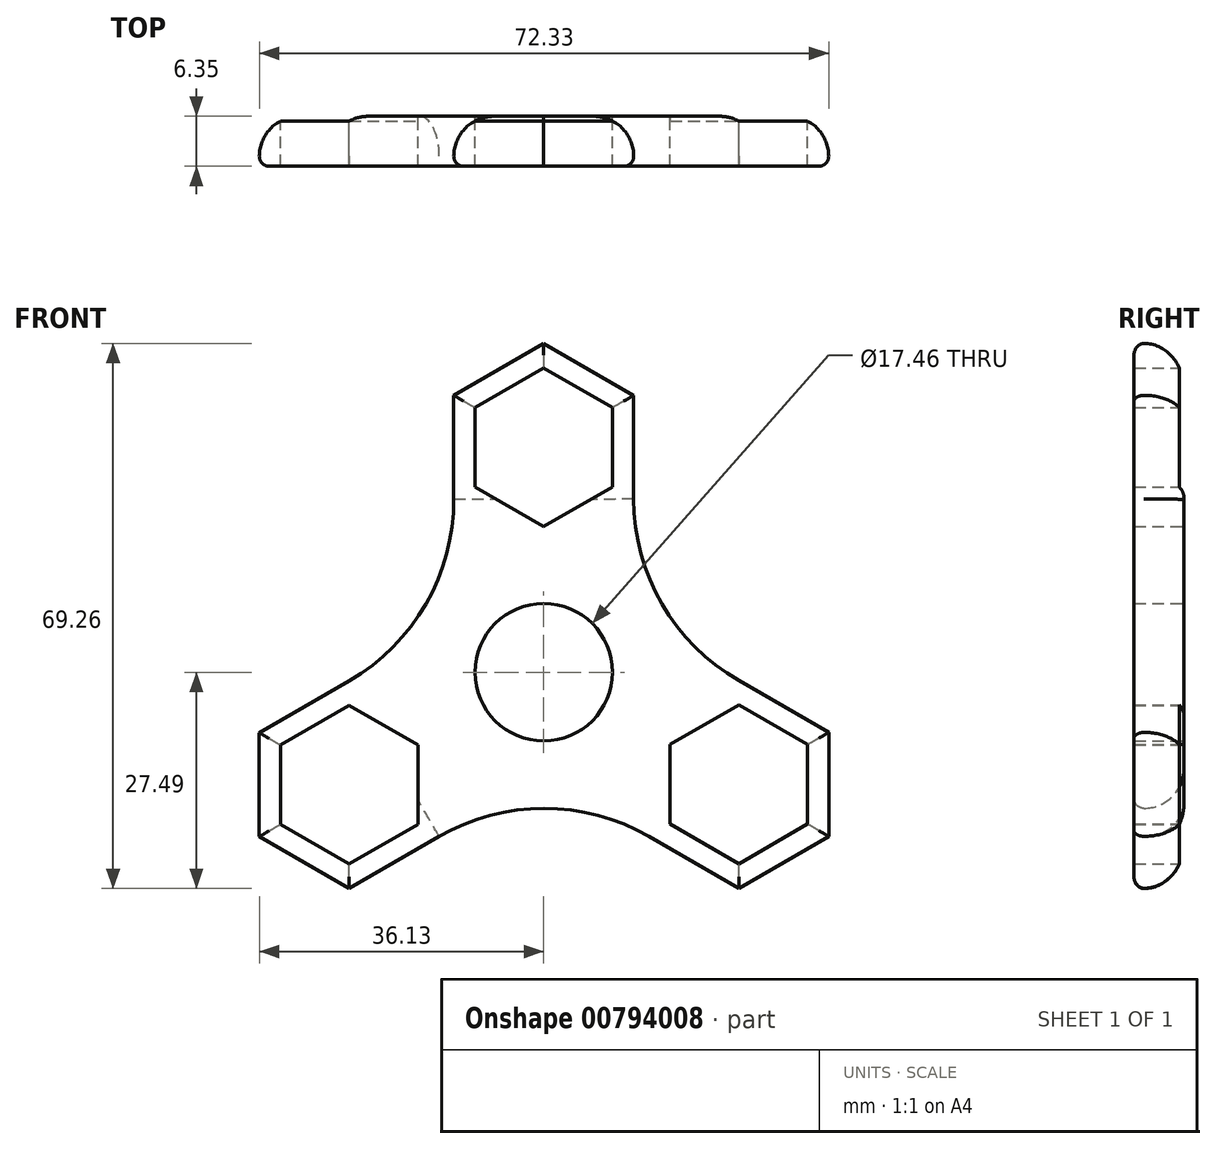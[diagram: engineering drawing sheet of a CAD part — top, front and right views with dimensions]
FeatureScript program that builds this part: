
annotation { "Feature Type Name" : "Feature", "Feature Type Description" : "" }
export const myFeature = defineFeature(function(context is Context, id is Id, definition is map)
    precondition{}
    {
        {
            var Q0;
            Q0=qCreatedBy(makeId("Front.planeOp"),FACE);
            var sketch = newSketch(context, id + "F0", { "sketchPlane" : qUnion([Q0])});
            skCircle(sketch, "E0", {"center": v(0, 0) * mm, "radius": 8.73 * mm});
            skCircle(sketch, "E1", {"center": v(0, 0) * mm, "radius": 14.29 * mm});
            skCircle(sketch, "E2.cCircle", {"center": v(0, 28.58) * mm, "radius": 8.74 * mm, "construction": true});
            skLineSegment(sketch, "E2.0", {"start": v(-8.74, 23.53) * mm, "end": v(-8.74, 33.62) * mm});
            skLineSegment(sketch, "E2.1", {"start": v(-8.74, 33.62) * mm, "end": v(0, 38.66) * mm});
            skLineSegment(sketch, "E2.2", {"start": v(0, 38.66) * mm, "end": v(8.74, 33.62) * mm});
            skLineSegment(sketch, "E2.3", {"start": v(8.74, 33.62) * mm, "end": v(8.74, 23.53) * mm});
            skLineSegment(sketch, "E2.4", {"start": v(8.74, 23.53) * mm, "end": v(0, 18.49) * mm});
            skLineSegment(sketch, "E2.5", {"start": v(0, 18.49) * mm, "end": v(-8.74, 23.53) * mm});
            skPoint(sketch, "E2.0.midPoint", {"position": v(-8.74, 28.58) * mm});
            skCircle(sketch, "E3.cCircle", {"center": v(0, 28.58) * mm, "radius": 11.43 * mm, "construction": true});
            skLineSegment(sketch, "E3.0", {"start": v(-11.43, 21.98) * mm, "end": v(-11.43, 35.17) * mm});
            skLineSegment(sketch, "E3.1", {"start": v(-11.43, 35.17) * mm, "end": v(0, 41.77) * mm});
            skLineSegment(sketch, "E3.2", {"start": v(0, 41.77) * mm, "end": v(11.43, 35.17) * mm});
            skLineSegment(sketch, "E3.3", {"start": v(11.43, 35.17) * mm, "end": v(11.43, 21.98) * mm});
            skLineSegment(sketch, "E3.4", {"start": v(11.43, 21.98) * mm, "end": v(0, 15.38) * mm});
            skLineSegment(sketch, "E3.5", {"start": v(0, 15.38) * mm, "end": v(-11.43, 21.98) * mm});
            skPoint(sketch, "E3.0.midPoint", {"position": v(-11.43, 28.58) * mm});
            skPoint(sketch, "E4.1.0", {"position": v(-18.99, -24.19) * mm});
            skCircle(sketch, "E4.1.1", {"center": v(-24.7, -14.29) * mm, "radius": 8.74 * mm, "construction": true});
            skLineSegment(sketch, "E4.1.2", {"start": v(-33.44, -19.33) * mm, "end": v(-33.44, -9.24) * mm});
            skLineSegment(sketch, "E4.1.3", {"start": v(-13.27, -7.69) * mm, "end": v(-13.27, -20.89) * mm});
            skLineSegment(sketch, "E4.1.4", {"start": v(-24.7, -1.09) * mm, "end": v(-13.27, -7.69) * mm});
            skLineSegment(sketch, "E4.1.5", {"start": v(-36.13, -7.69) * mm, "end": v(-24.7, -1.09) * mm});
            skLineSegment(sketch, "E4.1.6", {"start": v(-24.7, -24.38) * mm, "end": v(-33.44, -19.33) * mm});
            skLineSegment(sketch, "E4.1.7", {"start": v(-33.44, -9.24) * mm, "end": v(-24.7, -4.2) * mm});
            skLineSegment(sketch, "E4.1.8", {"start": v(-15.96, -9.24) * mm, "end": v(-15.96, -19.33) * mm});
            skCircle(sketch, "E4.1.9", {"center": v(-24.7, -14.29) * mm, "radius": 11.43 * mm, "construction": true});
            skLineSegment(sketch, "E4.1.10", {"start": v(-13.27, -20.89) * mm, "end": v(-24.7, -27.49) * mm});
            skLineSegment(sketch, "E4.1.11", {"start": v(-24.7, -27.49) * mm, "end": v(-36.13, -20.89) * mm});
            skLineSegment(sketch, "E4.1.12", {"start": v(-36.13, -20.89) * mm, "end": v(-36.13, -7.69) * mm});
            skPoint(sketch, "E4.1.13", {"position": v(-20.33, -21.85) * mm});
            skLineSegment(sketch, "E4.1.14", {"start": v(-15.96, -19.33) * mm, "end": v(-24.7, -24.38) * mm});
            skLineSegment(sketch, "E4.1.15", {"start": v(-24.7, -4.2) * mm, "end": v(-15.96, -9.24) * mm});
            skPoint(sketch, "E4.2.0", {"position": v(30.48, -4.35) * mm});
            skCircle(sketch, "E4.2.1", {"center": v(24.77, -14.25) * mm, "radius": 8.74 * mm, "construction": true});
            skLineSegment(sketch, "E4.2.2", {"start": v(33.5, -19.3) * mm, "end": v(24.77, -24.34) * mm});
            skLineSegment(sketch, "E4.2.3", {"start": v(13.34, -7.65) * mm, "end": v(24.77, -1.05) * mm});
            skLineSegment(sketch, "E4.2.4", {"start": v(13.34, -20.85) * mm, "end": v(13.34, -7.65) * mm});
            skLineSegment(sketch, "E4.2.5", {"start": v(24.77, -27.45) * mm, "end": v(13.34, -20.85) * mm});
            skLineSegment(sketch, "E4.2.6", {"start": v(33.5, -9.2) * mm, "end": v(33.5, -19.3) * mm});
            skLineSegment(sketch, "E4.2.7", {"start": v(24.77, -24.34) * mm, "end": v(16.03, -19.3) * mm});
            skLineSegment(sketch, "E4.2.8", {"start": v(16.03, -9.2) * mm, "end": v(24.77, -4.16) * mm});
            skCircle(sketch, "E4.2.9", {"center": v(24.77, -14.25) * mm, "radius": 11.43 * mm, "construction": true});
            skLineSegment(sketch, "E4.2.10", {"start": v(24.77, -1.05) * mm, "end": v(36.2, -7.65) * mm});
            skLineSegment(sketch, "E4.2.11", {"start": v(36.2, -7.65) * mm, "end": v(36.2, -20.85) * mm});
            skLineSegment(sketch, "E4.2.12", {"start": v(36.2, -20.85) * mm, "end": v(24.77, -27.45) * mm});
            skPoint(sketch, "E4.2.13", {"position": v(29.14, -6.68) * mm});
            skLineSegment(sketch, "E4.2.14", {"start": v(24.77, -4.16) * mm, "end": v(33.5, -9.2) * mm});
            skLineSegment(sketch, "E4.2.15", {"start": v(16.03, -19.3) * mm, "end": v(16.03, -9.2) * mm});
            skPoint(sketch, "E4.center", {"position": v(0.02, 0.01) * mm});
            skArc(sketch, "E5", {"start": v(-24.7, -1.09) * mm, "mid": v(-14.97, 8.66) * mm, "end": v(-11.43, 21.98) * mm});
            skArc(sketch, "E6", {"start": v(11.43, 21.98) * mm, "mid": v(15.02, 8.68) * mm, "end": v(24.77, -1.05) * mm});
            skArc(sketch, "E7", {"start": v(13.34, -20.85) * mm, "mid": v(0.03, -17.3) * mm, "end": v(-13.27, -20.89) * mm});
            skSolve(sketch);
        }
        {
            var Q0;
            Q0=qSketchRegion(id+"F0",true);
            var Q1;
            Q1=makeQuery(id+"F0.imprint","IMPRINT",FACE,{"disambiguationData":[TD([[makeQuery(id+"F0.imprint","IMPRINT",EDGE,{"derivedFrom":sQuery(id+"F0.wireOp",EDGE,"E0")}),-1.0]])]});
            extrude(context, id + "F1", {"entities" : qUnion([Q0, Q1]), "depth" : 6.35 * mm, "offsetDistance" : 25.4 * mm});
        }
        {
            var Q0;
            Q0=makeQuery(id+"F1.opExtrude","CAP_EDGE",EDGE,{"disambiguationData":[OSD([sQuery(id+"F0.wireOp",EDGE,"E3.0")])],"isStart":false});
            var Q1;
            Q1=makeQuery(id+"F1.opExtrude","CAP_EDGE",EDGE,{"disambiguationData":[OSD([sQuery(id+"F0.wireOp",EDGE,"E3.1")])],"isStart":false});
            var Q2;
            Q2=makeQuery(id+"F1.opExtrude","CAP_EDGE",EDGE,{"disambiguationData":[OSD([sQuery(id+"F0.wireOp",EDGE,"E3.2")])],"isStart":false});
            var Q3;
            Q3=makeQuery(id+"F1.opExtrude","CAP_EDGE",EDGE,{"disambiguationData":[OSD([sQuery(id+"F0.wireOp",EDGE,"E3.3")])],"isStart":false});
            var Q4;
            Q4=makeQuery(id+"F1.opExtrude","CAP_EDGE",EDGE,{"disambiguationData":[OSD([sQuery(id+"F0.wireOp",EDGE,"E4.2.10")])],"isStart":false});
            var Q5;
            Q5=makeQuery(id+"F1.opExtrude","CAP_EDGE",EDGE,{"disambiguationData":[OSD([sQuery(id+"F0.wireOp",EDGE,"E4.2.11")])],"isStart":false});
            var Q6;
            Q6=makeQuery(id+"F1.opExtrude","CAP_EDGE",EDGE,{"disambiguationData":[OSD([sQuery(id+"F0.wireOp",EDGE,"E4.2.12")])],"isStart":false});
            var Q7;
            Q7=makeQuery(id+"F1.opExtrude","CAP_EDGE",EDGE,{"disambiguationData":[OSD([sQuery(id+"F0.wireOp",EDGE,"E4.2.5")])],"isStart":false});
            var Q8;
            Q8=makeQuery(id+"F1.opExtrude","CAP_EDGE",EDGE,{"disambiguationData":[OSD([sQuery(id+"F0.wireOp",EDGE,"E4.1.10")])],"isStart":false});
            var Q9;
            Q9=makeQuery(id+"F1.opExtrude","CAP_EDGE",EDGE,{"disambiguationData":[OSD([sQuery(id+"F0.wireOp",EDGE,"E4.1.11")])],"isStart":false});
            var Q10;
            Q10=makeQuery(id+"F1.opExtrude","CAP_EDGE",EDGE,{"disambiguationData":[OSD([sQuery(id+"F0.wireOp",EDGE,"E4.1.12")])],"isStart":false});
            var Q11;
            Q11=makeQuery(id+"F1.opExtrude","CAP_EDGE",EDGE,{"disambiguationData":[OSD([sQuery(id+"F0.wireOp",EDGE,"E4.1.5")])],"isStart":false});
            fillet(context, id + "F2", {"entities" : qUnion([Q0, Q1, Q2, Q3, Q4, Q5, Q6, Q7, Q8, Q9, Q10, Q11]), "radius" : 1.27 * mm, "tangentPropagation" : true, "allowEdgeOverflow" : false});
        }
        {
            var Q0;
            Q0=makeQuery(id+"F1.opExtrude","CAP_EDGE",EDGE,{"disambiguationData":[OSD([sQuery(id+"F0.wireOp",EDGE,"E3.2")])],"isStart":true});
            var Q1;
            Q1=makeQuery(id+"F1.opExtrude","CAP_EDGE",EDGE,{"disambiguationData":[OSD([sQuery(id+"F0.wireOp",EDGE,"E3.1")])],"isStart":true});
            var Q2;
            Q2=makeQuery(id+"F1.opExtrude","CAP_EDGE",EDGE,{"disambiguationData":[OSD([sQuery(id+"F0.wireOp",EDGE,"E3.3")])],"isStart":true});
            var Q3;
            Q3=makeQuery(id+"F1.opExtrude","CAP_EDGE",EDGE,{"disambiguationData":[OSD([sQuery(id+"F0.wireOp",EDGE,"E6")])],"isStart":true});
            var Q4;
            Q4=makeQuery(id+"F1.opExtrude","CAP_EDGE",EDGE,{"disambiguationData":[OSD([sQuery(id+"F0.wireOp",EDGE,"E4.2.10")])],"isStart":true});
            var Q5;
            Q5=makeQuery(id+"F1.opExtrude","CAP_EDGE",EDGE,{"disambiguationData":[OSD([sQuery(id+"F0.wireOp",EDGE,"E4.2.11")])],"isStart":true});
            var Q6;
            Q6=makeQuery(id+"F1.opExtrude","CAP_EDGE",EDGE,{"disambiguationData":[OSD([sQuery(id+"F0.wireOp",EDGE,"E4.2.12")])],"isStart":true});
            var Q7;
            Q7=makeQuery(id+"F1.opExtrude","CAP_EDGE",EDGE,{"disambiguationData":[OSD([sQuery(id+"F0.wireOp",EDGE,"E4.2.5")])],"isStart":true});
            var Q8;
            Q8=makeQuery(id+"F1.opExtrude","CAP_EDGE",EDGE,{"disambiguationData":[OSD([sQuery(id+"F0.wireOp",EDGE,"E7")])],"isStart":true});
            var Q9;
            Q9=makeQuery(id+"F1.opExtrude","CAP_EDGE",EDGE,{"disambiguationData":[OSD([sQuery(id+"F0.wireOp",EDGE,"E4.1.10")])],"isStart":true});
            var Q10;
            Q10=makeQuery(id+"F1.opExtrude","CAP_EDGE",EDGE,{"disambiguationData":[OSD([sQuery(id+"F0.wireOp",EDGE,"E4.1.11")])],"isStart":true});
            var Q11;
            Q11=makeQuery(id+"F1.opExtrude","CAP_EDGE",EDGE,{"disambiguationData":[OSD([sQuery(id+"F0.wireOp",EDGE,"E4.1.12")])],"isStart":true});
            var Q12;
            Q12=makeQuery(id+"F1.opExtrude","CAP_EDGE",EDGE,{"disambiguationData":[OSD([sQuery(id+"F0.wireOp",EDGE,"E4.1.5")])],"isStart":true});
            var Q13;
            Q13=makeQuery(id+"F1.opExtrude","CAP_EDGE",EDGE,{"disambiguationData":[OSD([sQuery(id+"F0.wireOp",EDGE,"E5")])],"isStart":true});
            var Q14;
            Q14=makeQuery(id+"F1.opExtrude","CAP_EDGE",EDGE,{"disambiguationData":[OSD([sQuery(id+"F0.wireOp",EDGE,"E3.0")])],"isStart":true});
            fillet(context, id + "F3", {"entities" : qUnion([Q0, Q1, Q2, Q3, Q4, Q5, Q6, Q7, Q8, Q9, Q10, Q11, Q12, Q13, Q14]), "radius" : 5.08 * mm, "tangentPropagation" : true, "allowEdgeOverflow" : false});
        }
    });
